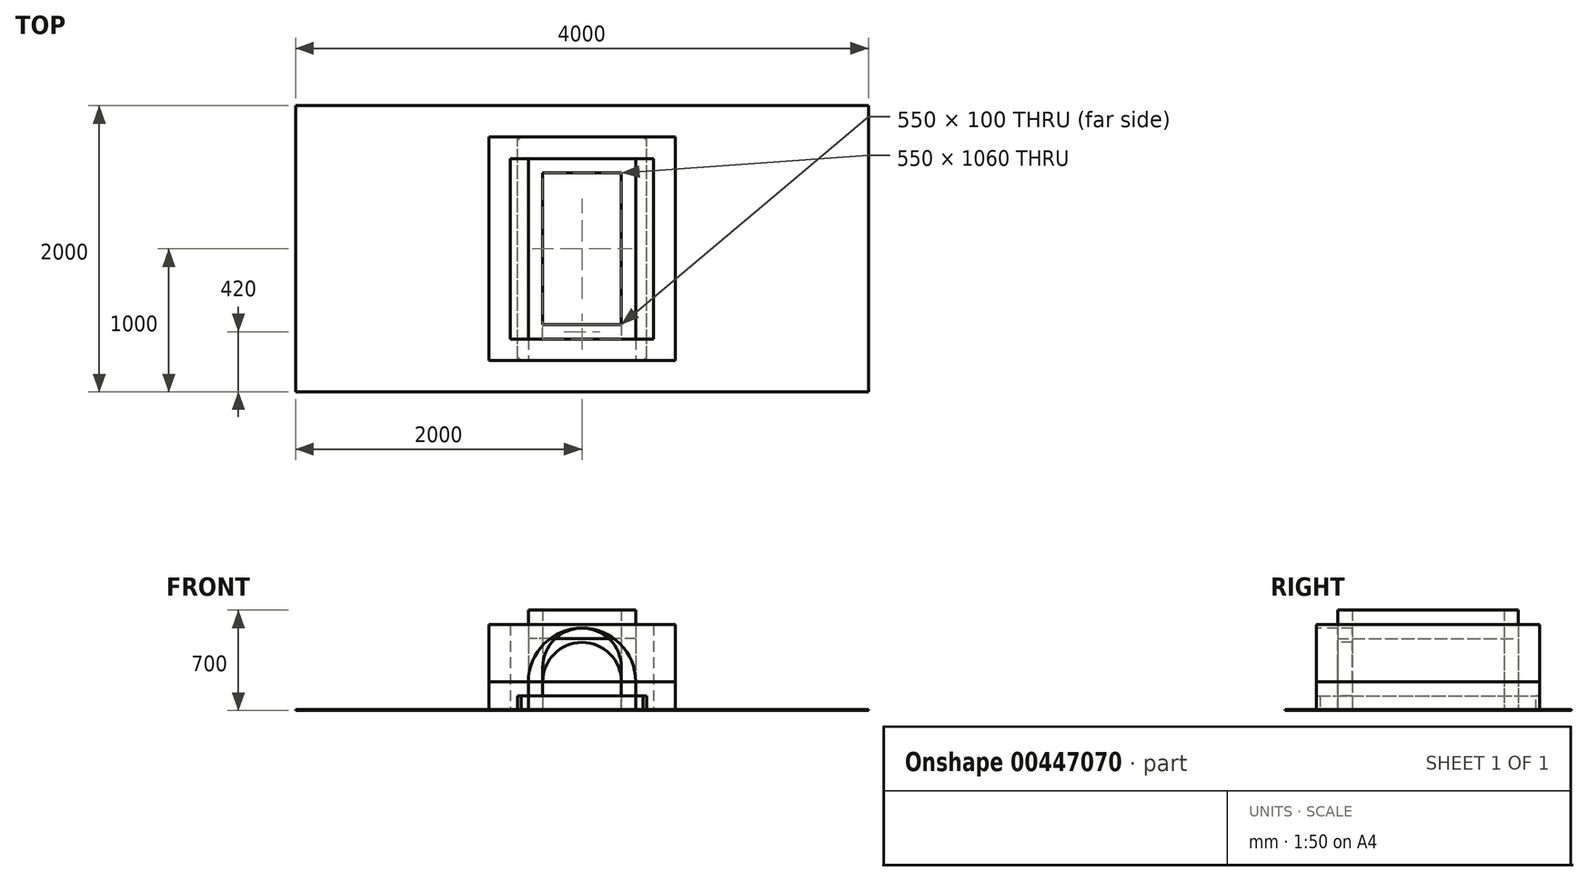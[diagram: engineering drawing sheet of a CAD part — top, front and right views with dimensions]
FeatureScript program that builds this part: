
annotation { "Feature Type Name" : "Feature", "Feature Type Description" : "" }
export const myFeature = defineFeature(function(context is Context, id is Id, definition is map)
    precondition{}
    {
        {
            var Q0;
            Q0=qCreatedBy(makeId("Top.planeOp"),FACE);
            var sketch = newSketch(context, id + "F0", { "sketchPlane" : qUnion([Q0])});
            skLineSegment(sketch, "E0.bottom", {"start": v(650, -780) * mm, "end": v(-650, -780) * mm});
            skLineSegment(sketch, "E0.top", {"start": v(650, 780) * mm, "end": v(-650, 780) * mm});
            skLineSegment(sketch, "E0.left", {"start": v(650, -780) * mm, "end": v(650, 780) * mm});
            skLineSegment(sketch, "E0.right", {"start": v(-650, -780) * mm, "end": v(-650, 780) * mm});
            skPoint(sketch, "E0.middle", {"position": v(0, 0) * mm});
            skSolve(sketch);
        }
        {
            var Q0;
            Q0=makeQuery(id+"F0.imprint","IMPRINT",FACE,{"disambiguationData":[TD([[makeQuery(id+"F0.imprint","IMPRINT",EDGE,{"derivedFrom":sQuery(id+"F0.wireOp",EDGE,"E0.bottom")}),-1.0]])]});
            extrude(context, id + "F1", {"entities" : qUnion([Q0]), "depth" : 200 * mm});
        }
        {
            var Q0;
            Q0=qCreatedBy(makeId("Top.planeOp"),FACE);
            var sketch = newSketch(context, id + "F2", { "sketchPlane" : qUnion([Q0])});
            skLineSegment(sketch, "E1.bottom", {"start": v(650, -780) * mm, "end": v(-650, -780) * mm});
            skLineSegment(sketch, "E1.top", {"start": v(650, 780) * mm, "end": v(-650, 780) * mm});
            skLineSegment(sketch, "E1.left", {"start": v(650, -780) * mm, "end": v(650, 780) * mm});
            skLineSegment(sketch, "E1.right", {"start": v(-650, -780) * mm, "end": v(-650, 780) * mm});
            skPoint(sketch, "E1.middle", {"position": v(0, 0) * mm});
            skLineSegment(sketch, "E2.0", {"start": v(500, 630) * mm, "end": v(-500, 630) * mm});
            skLineSegment(sketch, "E2.1", {"start": v(500, -630) * mm, "end": v(500, 630) * mm});
            skLineSegment(sketch, "E2.2", {"start": v(500, -630) * mm, "end": v(-500, -630) * mm});
            skLineSegment(sketch, "E2.3", {"start": v(-500, -630) * mm, "end": v(-500, 630) * mm});
            skSolve(sketch);
        }
        {
            var Q0;
            Q0=makeQuery(id+"F2.imprint","IMPRINT",FACE,{"disambiguationData":[TD([[makeQuery(id+"F2.imprint","IMPRINT",EDGE,{"derivedFrom":sQuery(id+"F2.wireOp",EDGE,"E1.bottom")}),-1.0]])]});
            extrude(context, id + "F3", {"entities" : qUnion([Q0]), "depth" : 600 * mm});
        }
        {
            var Q0;
            Q0=makeQuery(id+"F3.opExtrude","SWEPT_FACE",FACE,{"disambiguationData":[OSD([sQuery(id+"F2.wireOp",EDGE,"E1.bottom")])]});
            var sketch = newSketch(context, id + "F4", { "sketchPlane" : qUnion([Q0])});
            skLineSegment(sketch, "E3.bottom", {"start": v(-375, 0) * mm, "end": v(375, 0) * mm});
            skLineSegment(sketch, "E3.top", {"start": v(0, 200) * mm, "end": v(0, 200) * mm});
            skLineSegment(sketch, "E3.left", {"start": v(-375, 0) * mm, "end": v(-375, 200) * mm});
            skLineSegment(sketch, "E3.right", {"start": v(375, 0) * mm, "end": v(375, 200) * mm});
            skLineSegment(sketch, "E4", {"start": v(-375, 200) * mm, "end": v(0, 200) * mm, "construction": true});
            skLineSegment(sketch, "E5", {"start": v(0, 200) * mm, "end": v(375, 200) * mm, "construction": true});
            skLineSegment(sketch, "E6", {"start": v(0, 200) * mm, "end": v(0, 0) * mm, "construction": true});
            skArc(sketch, "E7", {"start": v(-375, 200) * mm, "mid": v(0, 575) * mm, "end": v(375, 200) * mm});
            skLineSegment(sketch, "E8", {"start": v(0, 575) * mm, "end": v(0, 200) * mm, "construction": true});
            skSolve(sketch);
        }
        {
            var Q0;
            Q0=makeQuery(id+"F4.imprint","IMPRINT",FACE,{"disambiguationData":[TD([[makeQuery(id+"F4.imprint","IMPRINT",EDGE,{"derivedFrom":sQuery(id+"F4.wireOp",EDGE,"E3.bottom")}),-1.0]])]});
            extrude(context, id + "F5", {"entities" : qUnion([Q0]), "operationType" : NewBodyOperationType.REMOVE, "endBound" : BoundingType.UP_TO_NEXT, "oppositeDirection" : true, "depth" : 25 * mm});
        }
        {
            var Q0;
            Q0=qCreatedBy(makeId("Top.planeOp"),FACE);
            var sketch = newSketch(context, id + "F6", { "sketchPlane" : qUnion([Q0])});
            skLineSegment(sketch, "E9.bottom", {"start": v(375, -630) * mm, "end": v(-375, -630) * mm});
            skLineSegment(sketch, "E9.top", {"start": v(375, 630) * mm, "end": v(-375, 630) * mm});
            skLineSegment(sketch, "E9.left", {"start": v(375, -630) * mm, "end": v(375, 630) * mm});
            skLineSegment(sketch, "E9.right", {"start": v(-375, -630) * mm, "end": v(-375, 630) * mm});
            skPoint(sketch, "E9.middle", {"position": v(0, 0) * mm});
            skLineSegment(sketch, "E10.0", {"start": v(275, 530) * mm, "end": v(-275, 530) * mm});
            skLineSegment(sketch, "E10.1", {"start": v(275, -530) * mm, "end": v(275, 530) * mm});
            skLineSegment(sketch, "E10.2", {"start": v(275, -530) * mm, "end": v(-275, -530) * mm});
            skLineSegment(sketch, "E10.3", {"start": v(-275, -530) * mm, "end": v(-275, 530) * mm});
            skSolve(sketch);
        }
        {
            var Q0;
            Q0=makeQuery(id+"F6.imprint","IMPRINT",FACE,{"disambiguationData":[TD([[makeQuery(id+"F6.imprint","IMPRINT",EDGE,{"derivedFrom":sQuery(id+"F6.wireOp",EDGE,"E9.bottom")}),-1.0]])]});
            extrude(context, id + "F7", {"entities" : qUnion([Q0]), "depth" : 700 * mm});
        }
        {
            var Q0;
            Q0=makeQuery(id+"F7.opExtrude","SWEPT_FACE",FACE,{"disambiguationData":[OSD([sQuery(id+"F6.wireOp",EDGE,"E9.bottom")])]});
            var sketch = newSketch(context, id + "F8", { "sketchPlane" : qUnion([Q0])});
            skLineSegment(sketch, "E11", {"start": v(-275, 0) * mm, "end": v(-275, 300) * mm});
            skLineSegment(sketch, "E12", {"start": v(-275, 300) * mm, "end": v(0, 300) * mm, "construction": true});
            skLineSegment(sketch, "E13", {"start": v(0, 300) * mm, "end": v(275, 300) * mm, "construction": true});
            skLineSegment(sketch, "E14", {"start": v(275, 300) * mm, "end": v(275, 0) * mm});
            skLineSegment(sketch, "E15", {"start": v(0, 300) * mm, "end": v(0, 0) * mm, "construction": true});
            skArc(sketch, "E16", {"start": v(-275, 300) * mm, "mid": v(0, 575) * mm, "end": v(275, 300) * mm});
            skLineSegment(sketch, "E17", {"start": v(0, 575) * mm, "end": v(0, 300) * mm, "construction": true});
            skSolve(sketch);
        }
        {
            var Q0;
            {var subQ0=sQuery(id+"F8.wireOp",EDGE,"E11");Q0=makeQuery(id+"F8.imprint","IMPRINT",FACE,{"disambiguationData":[TD([[makeQuery(id+"F8.imprint","IMPRINT",EDGE,{"derivedFrom":subQ0}),-1.0]])]});}
            extrude(context, id + "F9", {"entities" : qUnion([Q0]), "operationType" : NewBodyOperationType.REMOVE, "endBound" : BoundingType.UP_TO_NEXT, "oppositeDirection" : true, "depth" : 25 * mm});
        }
        {
            var Q0;
            Q0=qCreatedBy(makeId("Top.planeOp"),FACE);
            var sketch = newSketch(context, id + "F10", { "sketchPlane" : qUnion([Q0])});
            skLineSegment(sketch, "E18.bottom", {"start": v(450, -780) * mm, "end": v(-450, -780) * mm});
            skLineSegment(sketch, "E18.top", {"start": v(450, 780) * mm, "end": v(-450, 780) * mm});
            skLineSegment(sketch, "E18.left", {"start": v(450, -780) * mm, "end": v(450, 780) * mm});
            skLineSegment(sketch, "E18.right", {"start": v(-450, -780) * mm, "end": v(-450, 780) * mm});
            skPoint(sketch, "E18.middle", {"position": v(0, 0) * mm});
            skSolve(sketch);
        }
        {
            var Q0;
            Q0=makeQuery(id+"F10.imprint","IMPRINT",FACE,{"disambiguationData":[TD([[makeQuery(id+"F10.imprint","IMPRINT",EDGE,{"derivedFrom":sQuery(id+"F10.wireOp",EDGE,"E18.bottom")}),-1.0]])]});
            extrude(context, id + "F11", {"entities" : qUnion([Q0]), "depth" : 100 * mm});
        }
        {
            var Q0;
            Q0=makeQuery(id+"F11.opExtrude","SWEPT_EDGE",EDGE,{"disambiguationData":[OSD([sQuery(id+"F10.wireOp",EDGE,"E18.bottom"),sQuery(id+"F10.wireOp",EDGE,"E18.left")])]});
            var Q1;
            Q1=makeQuery(id+"F11.opExtrude","SWEPT_EDGE",EDGE,{"disambiguationData":[OSD([sQuery(id+"F10.wireOp",EDGE,"E18.top"),sQuery(id+"F10.wireOp",EDGE,"E18.left")])]});
            chamfer(context, id + "F12", {"entities" : qUnion([Q0, Q1]), "width" : 25 * mm, "tangentPropagation" : true});
        }
        {
            var Q0;
            Q0=qCreatedBy(makeId("Top.planeOp"),FACE);
            var sketch = newSketch(context, id + "F13", { "sketchPlane" : qUnion([Q0])});
            skLineSegment(sketch, "E19.bottom", {"start": v(375, -630) * mm, "end": v(-375, -630) * mm});
            skLineSegment(sketch, "E19.top", {"start": v(375, 630) * mm, "end": v(-375, 630) * mm});
            skLineSegment(sketch, "E19.left", {"start": v(375, -630) * mm, "end": v(375, 630) * mm});
            skLineSegment(sketch, "E19.right", {"start": v(-375, -630) * mm, "end": v(-375, 630) * mm});
            skPoint(sketch, "E19.middle", {"position": v(0, 0) * mm});
            skLineSegment(sketch, "E20.0", {"start": v(275, 530) * mm, "end": v(-275, 530) * mm});
            skLineSegment(sketch, "E20.1", {"start": v(275, -530) * mm, "end": v(275, 530) * mm});
            skLineSegment(sketch, "E20.2", {"start": v(275, -530) * mm, "end": v(-275, -530) * mm});
            skLineSegment(sketch, "E20.3", {"start": v(-275, -530) * mm, "end": v(-275, 530) * mm});
            skSolve(sketch);
        }
        {
            var Q0;
            Q0=makeQuery(id+"F13.imprint","IMPRINT",FACE,{"disambiguationData":[TD([[makeQuery(id+"F13.imprint","IMPRINT",EDGE,{"derivedFrom":sQuery(id+"F13.wireOp",EDGE,"E19.bottom")}),-1.0]])]});
            extrude(context, id + "F14", {"entities" : qUnion([Q0]), "depth" : 500 * mm});
        }
        {
            var Q0;
            Q0=makeQuery(id+"F14.opExtrude","SWEPT_FACE",FACE,{"disambiguationData":[OSD([sQuery(id+"F13.wireOp",EDGE,"E19.bottom")])]});
            var sketch = newSketch(context, id + "F15", { "sketchPlane" : qUnion([Q0])});
            skLineSegment(sketch, "E21", {"start": v(-275, 0) * mm, "end": v(-275, 200) * mm});
            skLineSegment(sketch, "E22", {"start": v(-275, 200) * mm, "end": v(0, 200) * mm, "construction": true});
            skLineSegment(sketch, "E23", {"start": v(0, 200) * mm, "end": v(275, 200) * mm, "construction": true});
            skLineSegment(sketch, "E24", {"start": v(275, 200) * mm, "end": v(275, 0) * mm});
            skLineSegment(sketch, "E25", {"start": v(0, 200) * mm, "end": v(0, 0) * mm, "construction": true});
            skArc(sketch, "E26", {"start": v(-275, 200) * mm, "mid": v(0, 475) * mm, "end": v(275, 200) * mm});
            skLineSegment(sketch, "E27", {"start": v(0, 475) * mm, "end": v(0, 200) * mm, "construction": true});
            skSolve(sketch);
        }
        {
            var Q0;
            {var subQ0=sQuery(id+"F15.wireOp",EDGE,"E21");Q0=makeQuery(id+"F15.imprint","IMPRINT",FACE,{"disambiguationData":[TD([[makeQuery(id+"F15.imprint","IMPRINT",EDGE,{"derivedFrom":subQ0}),-1.0]])]});}
            extrude(context, id + "F16", {"entities" : qUnion([Q0]), "operationType" : NewBodyOperationType.REMOVE, "endBound" : BoundingType.UP_TO_NEXT, "oppositeDirection" : true, "depth" : 25 * mm});
        }
        {
            var Q0;
            Q0=qCreatedBy(makeId("Top.planeOp"),FACE);
            var sketch = newSketch(context, id + "F17", { "sketchPlane" : qUnion([Q0])});
            skLineSegment(sketch, "E28.bottom", {"start": v(450, -780) * mm, "end": v(-450, -780) * mm});
            skLineSegment(sketch, "E28.top", {"start": v(450, 780) * mm, "end": v(-450, 780) * mm});
            skLineSegment(sketch, "E28.left", {"start": v(450, -780) * mm, "end": v(450, 780) * mm});
            skLineSegment(sketch, "E28.right", {"start": v(-450, -780) * mm, "end": v(-450, 780) * mm});
            skPoint(sketch, "E28.middle", {"position": v(0, 0) * mm});
            skSolve(sketch);
        }
        {
            var Q0;
            Q0=makeQuery(id+"F17.imprint","IMPRINT",FACE,{"disambiguationData":[TD([[makeQuery(id+"F17.imprint","IMPRINT",EDGE,{"derivedFrom":sQuery(id+"F17.wireOp",EDGE,"E28.bottom")}),-1.0]])]});
            extrude(context, id + "F18", {"entities" : qUnion([Q0]), "depth" : 100 * mm});
        }
        {
            var Q0;
            Q0=makeQuery(id+"F18.opExtrude","SWEPT_EDGE",EDGE,{"disambiguationData":[OSD([sQuery(id+"F17.wireOp",EDGE,"E28.bottom"),sQuery(id+"F17.wireOp",EDGE,"E28.right")])]});
            var Q1;
            Q1=makeQuery(id+"F18.opExtrude","SWEPT_EDGE",EDGE,{"disambiguationData":[OSD([sQuery(id+"F17.wireOp",EDGE,"E28.top"),sQuery(id+"F17.wireOp",EDGE,"E28.right")])]});
            chamfer(context, id + "F19", {"entities" : qUnion([Q0, Q1]), "width" : 25 * mm, "tangentPropagation" : true});
        }
        {
            var Q0;
            Q0=qCreatedBy(makeId("Top.planeOp"),FACE);
            var sketch = newSketch(context, id + "F20", { "sketchPlane" : qUnion([Q0])});
            skLineSegment(sketch, "E29.bottom", {"start": v(2000, -1000) * mm, "end": v(-2000, -1000) * mm});
            skLineSegment(sketch, "E29.top", {"start": v(2000, 1000) * mm, "end": v(-2000, 1000) * mm});
            skLineSegment(sketch, "E29.left", {"start": v(2000, -1000) * mm, "end": v(2000, 1000) * mm});
            skLineSegment(sketch, "E29.right", {"start": v(-2000, -1000) * mm, "end": v(-2000, 1000) * mm});
            skPoint(sketch, "E29.middle", {"position": v(0, 0) * mm});
            skSolve(sketch);
        }
        {
            var Q0;
            Q0=makeQuery(id+"F20.imprint","IMPRINT",FACE,{"disambiguationData":[TD([[makeQuery(id+"F20.imprint","IMPRINT",EDGE,{"derivedFrom":sQuery(id+"F20.wireOp",EDGE,"E29.bottom")}),-1.0]])]});
            extrude(context, id + "F21", {"entities" : qUnion([Q0]), "depth" : 5 * mm});
        }
    });
